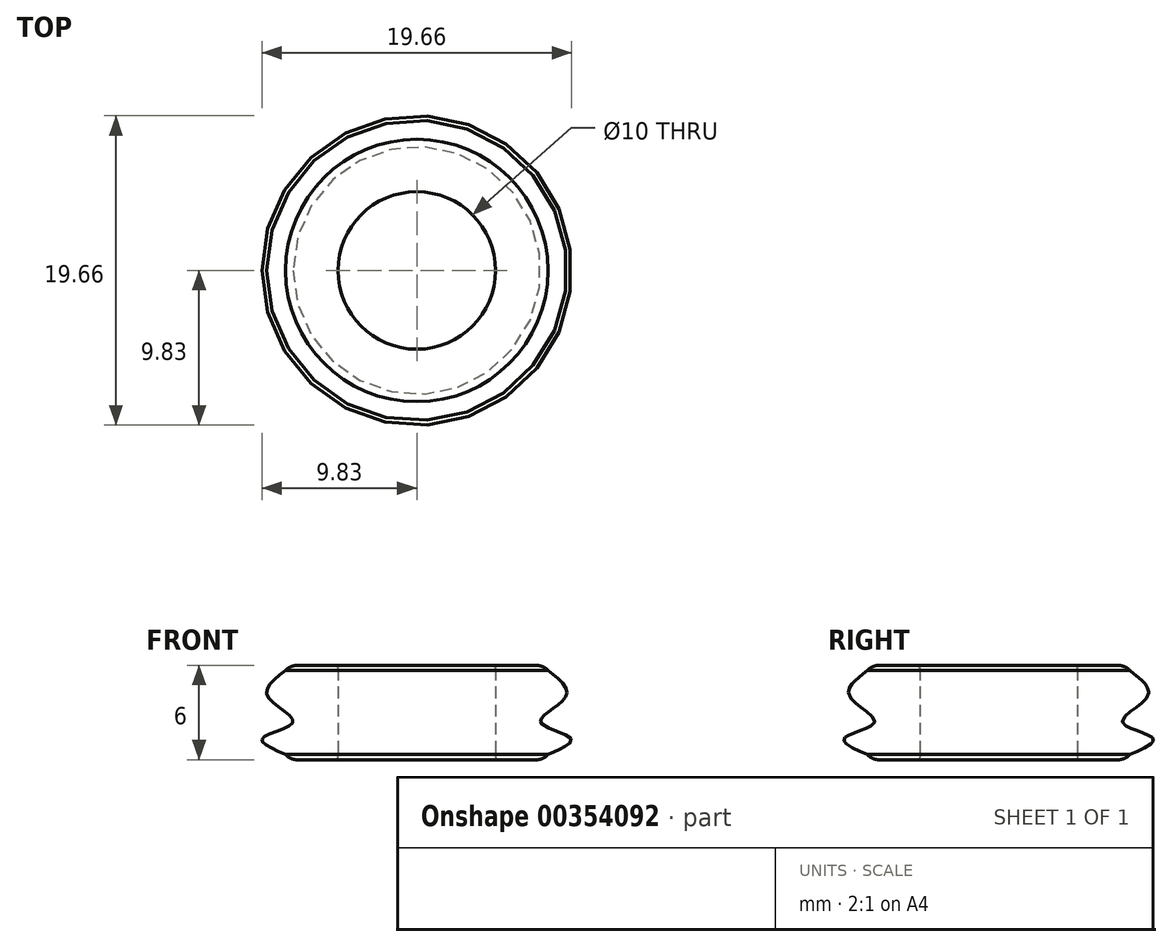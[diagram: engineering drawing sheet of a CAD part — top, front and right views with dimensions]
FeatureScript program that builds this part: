
annotation { "Feature Type Name" : "Feature", "Feature Type Description" : "" }
export const myFeature = defineFeature(function(context is Context, id is Id, definition is map)
    precondition{}
    {
        {
            var Q0;
            Q0=qCreatedBy(makeId("Front.planeOp"),FACE);
            var sketch = newSketch(context, id + "F0", { "sketchPlane" : qUnion([Q0])});
            skLineSegment(sketch, "E0", {"start": v(0, 0.2) * mm, "end": v(0, 5.8) * mm});
            skLineSegment(sketch, "E1", {"start": v(-0.2, 0) * mm, "end": v(-2.6, 0) * mm});
            skLineSegment(sketch, "E2", {"start": v(-0.2, 6) * mm, "end": v(-2.6, 6) * mm});
            skPoint(sketch, "E3.visualSharp", {"position": v(-3, 6) * mm});
            skArc(sketch, "E3.filletArc", {"start": v(-2.6, 6) * mm, "mid": v(-3, 5.91) * mm, "end": v(-3.34, 5.67) * mm});
            skPoint(sketch, "E4.visualSharp", {"position": v(-3, 0) * mm});
            skArc(sketch, "E4.filletArc", {"start": v(-3.34, 0.33) * mm, "mid": v(-3, 0.09) * mm, "end": v(-2.6, 0) * mm});
            skPoint(sketch, "E5.visualSharp", {"position": v(0, 0) * mm});
            skArc(sketch, "E5.filletArc", {"start": v(-0.2, 0) * mm, "mid": v(-0.06, 0.06) * mm, "end": v(0, 0.2) * mm});
            skPoint(sketch, "E6.visualSharp", {"position": v(0, 6) * mm});
            skArc(sketch, "E6.filletArc", {"start": v(0, 5.8) * mm, "mid": v(-0.06, 5.94) * mm, "end": v(-0.2, 6) * mm});
            skLineSegment(sketch, "E7.0", {"start": v(5, 0.2) * mm, "end": v(5, 5.8) * mm});
            skFitSpline(sketch, "E8", {"points": [v(-3.34, 5.67) * mm, v(-4.47, 4.04) * mm, v(-2.87, 2.4) * mm, v(-4.8, 1.37) * mm, v(-3.34, 0.33) * mm], "startDerivative": vector(-8.63, -6.57) * mm, "endDerivative": vector(10.87, -4.72) * mm});
            skSolve(sketch);
        }
        {
            var Q0;
            Q0=makeQuery(id+"F0.imprint","IMPRINT",FACE,{"disambiguationData":[TD([[makeQuery(id+"F0.imprint","IMPRINT",EDGE,{"derivedFrom":sQuery(id+"F0.wireOp",EDGE,"E0")}),1.0]])]});
            var Q1;
            Q1=sQuery(id+"F0.wireOp",EDGE,"E7.0");
            revolve(context, id + "F1", {"entities" : qUnion([Q0]), "axis" : qUnion([Q1]), "revolveType" : RevolveType.FULL});
        }
    });
